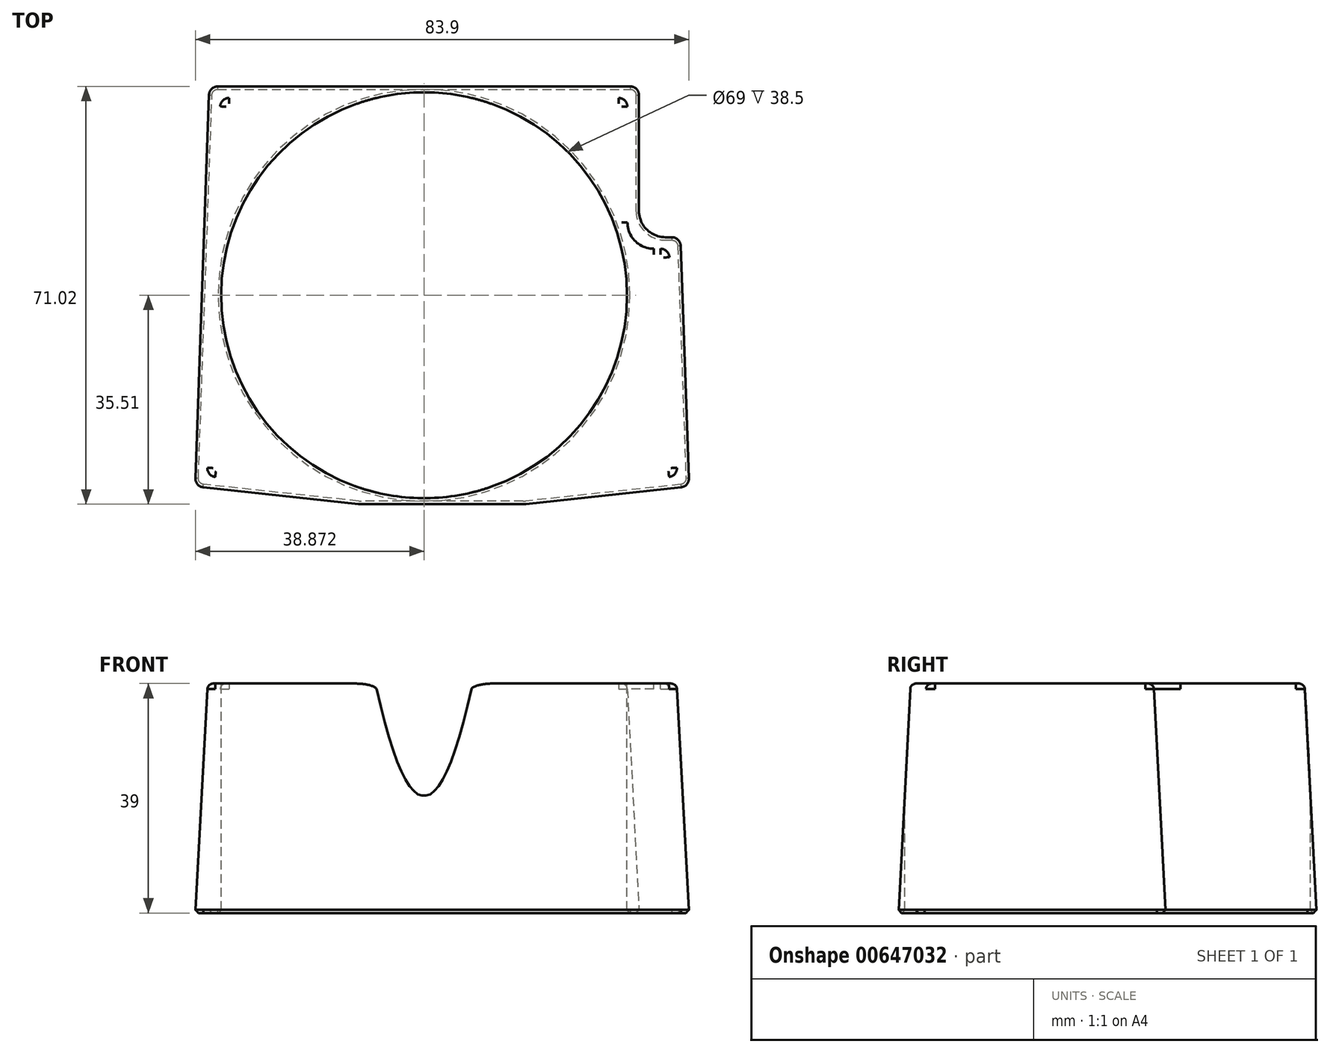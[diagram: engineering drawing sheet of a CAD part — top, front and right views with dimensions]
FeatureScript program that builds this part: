
annotation { "Feature Type Name" : "Feature", "Feature Type Description" : "" }
export const myFeature = defineFeature(function(context is Context, id is Id, definition is map)
    precondition{}
    {
        {
            var Q0;
            Q0=qCreatedBy(makeId("Top.planeOp"),FACE);
            var sketch = newSketch(context, id + "F0", { "sketchPlane" : qUnion([Q0])});
            skCircle(sketch, "E0", {"center": v(14.03, -35.08) * mm, "radius": 9.35 * mm});
            skCircle(sketch, "E1", {"center": v(-27.61, -12.6) * mm, "radius": 3.2 * mm});
            skCircle(sketch, "E2", {"center": v(29.9, -58.2) * mm, "radius": 3.2 * mm});
            skLineSegment(sketch, "E3", {"start": v(-40.06, 0) * mm, "end": v(33.94, 0) * mm});
            skLineSegment(sketch, "E4", {"start": v(42.5, -68.93) * mm, "end": v(14.3, -71.97) * mm});
            skLineSegment(sketch, "E5", {"start": v(13.76, -72) * mm, "end": v(-13.76, -72) * mm});
            skLineSegment(sketch, "E6", {"start": v(-14.3, -71.97) * mm, "end": v(-42.5, -68.93) * mm});
            skLineSegment(sketch, "E7", {"start": v(-42.5, -68.93) * mm, "end": v(-40.06, 0) * mm});
            skCircle(sketch, "E8", {"center": v(-27.61, -12.6) * mm, "radius": 1.2 * mm});
            skCircle(sketch, "E9", {"center": v(29.9, -58.2) * mm, "radius": 1.2 * mm});
            skCircle(sketch, "E10", {"center": v(14.03, -35.08) * mm, "radius": 3.1 * mm});
            skLineSegment(sketch, "E11", {"start": v(0, -72) * mm, "end": v(0, 0) * mm, "construction": true});
            skLineSegment(sketch, "E12.MirrorCS", {"start": v(42.5, -68.93) * mm, "end": v(40.06, 0) * mm});
            skLineSegment(sketch, "E13", {"start": v(40.06, 0) * mm, "end": v(33.94, 0) * mm});
            skPoint(sketch, "E14.visualSharp", {"position": v(14.03, -72) * mm});
            skArc(sketch, "E14.filletArc", {"start": v(13.76, -72) * mm, "mid": v(14.03, -72) * mm, "end": v(14.3, -71.97) * mm});
            skPoint(sketch, "E15.visualSharp", {"position": v(-14.03, -72) * mm});
            skArc(sketch, "E15.filletArc", {"start": v(-14.3, -71.97) * mm, "mid": v(-14.03, -72) * mm, "end": v(-13.76, -72) * mm});
            skLineSegment(sketch, "E16", {"start": v(33.94, 0) * mm, "end": v(33.94, -25.65) * mm});
            skLineSegment(sketch, "E17", {"start": v(33.94, -25.65) * mm, "end": v(40.97, -25.65) * mm});
            skLineSegment(sketch, "E18", {"start": v(0, 0) * mm, "end": v(0, 0.97) * mm});
            skSolve(sketch);
        }
        {
            var Q0;
            Q0=makeQuery(id+"F0.imprint","IMPRINT",FACE,{"disambiguationData":[TD([[makeQuery(id+"F0.imprint","IMPRINT",EDGE,{"derivedFrom":sQuery(id+"F0.wireOp",EDGE,"E0")}),-1.0]])]});
            var Q1;
            Q1=makeQuery(id+"F0.imprint","IMPRINT",FACE,{"disambiguationData":[TD([[makeQuery(id+"F0.imprint","IMPRINT",EDGE,{"derivedFrom":sQuery(id+"F0.wireOp",EDGE,"E0")}),1.0]])]});
            var Q2;
            Q2=makeQuery(id+"F0.imprint","IMPRINT",FACE,{"disambiguationData":[TD([[makeQuery(id+"F0.imprint","IMPRINT",EDGE,{"derivedFrom":sQuery(id+"F0.wireOp",EDGE,"E10")}),1.0]])]});
            var Q3;
            Q3=makeQuery(id+"F0.imprint","IMPRINT",FACE,{"disambiguationData":[TD([[makeQuery(id+"F0.imprint","IMPRINT",EDGE,{"derivedFrom":sQuery(id+"F0.wireOp",EDGE,"E8")}),1.0]])]});
            var Q4;
            Q4=makeQuery(id+"F0.imprint","IMPRINT",FACE,{"disambiguationData":[TD([[makeQuery(id+"F0.imprint","IMPRINT",EDGE,{"derivedFrom":sQuery(id+"F0.wireOp",EDGE,"E1")}),1.0]])]});
            var Q5;
            Q5=makeQuery(id+"F0.imprint","IMPRINT",FACE,{"disambiguationData":[TD([[makeQuery(id+"F0.imprint","IMPRINT",EDGE,{"derivedFrom":sQuery(id+"F0.wireOp",EDGE,"E2")}),1.0]])]});
            var Q6;
            Q6=makeQuery(id+"F0.imprint","IMPRINT",FACE,{"disambiguationData":[TD([[makeQuery(id+"F0.imprint","IMPRINT",EDGE,{"derivedFrom":sQuery(id+"F0.wireOp",EDGE,"E9")}),1.0]])]});
            extrude(context, id + "F1", {"entities" : qUnion([Q0, Q1, Q2, Q3, Q4, Q5, Q6]), "oppositeDirection" : true, "depth" : 39 * mm, "offsetDistance" : 25 * mm, "hasDraft" : true, "draftAngle" : 3 * degree});
        }
        {
            var Q0;
            Q0=makeQuery(id+"F1.opExtrude","SWEPT_EDGE",EDGE,{"disambiguationData":[OSD([sQuery(id+"F0.wireOp",EDGE,"E3"),sQuery(id+"F0.wireOp",EDGE,"E7")])]});
            var Q1;
            Q1=makeQuery(id+"F1.opExtrude","SWEPT_EDGE",EDGE,{"disambiguationData":[OSD([sQuery(id+"F0.wireOp",EDGE,"E3"),sQuery(id+"F0.wireOp",EDGE,"E13"),sQuery(id+"F0.wireOp",EDGE,"E16")])]});
            var Q2;
            Q2=makeQuery(id+"F1.opExtrude","SWEPT_EDGE",EDGE,{"disambiguationData":[OSD([sQuery(id+"F0.wireOp",EDGE,"E6"),sQuery(id+"F0.wireOp",EDGE,"E7")])]});
            var Q3;
            Q3=makeQuery(id+"F1.opExtrude","SWEPT_EDGE",EDGE,{"disambiguationData":[OSD([sQuery(id+"F0.wireOp",EDGE,"E4"),sQuery(id+"F0.wireOp",EDGE,"E12.MirrorCS")])]});
            var Q4;
            Q4=makeQuery(id+"F1.opExtrude","SWEPT_EDGE",EDGE,{"disambiguationData":[OSD([sQuery(id+"F0.wireOp",EDGE,"E12.MirrorCS"),sQuery(id+"F0.wireOp",EDGE,"E17")])]});
            fillet(context, id + "F2", {"entities" : qUnion([Q0, Q1, Q2, Q3, Q4]), "radius" : 4 * mm, "tangentPropagation" : true, "allowEdgeOverflow" : false});
        }
        {
            var Q0;
            Q0=makeQuery(id+"F1.opExtrude","SWEPT_EDGE",EDGE,{"disambiguationData":[OSD([sQuery(id+"F0.wireOp",EDGE,"E16"),sQuery(id+"F0.wireOp",EDGE,"E17")])]});
            fillet(context, id + "F3", {"entities" : qUnion([Q0]), "radius" : 2 * mm, "tangentPropagation" : true, "allowEdgeOverflow" : false});
        }
        {
            var Q0;
            Q0=makeQuery(id+"F1.opExtrude","SWEPT_BODY",BODY,{"disambiguationData":[OSD([sQuery(id+"F0.wireOp",EDGE,"E3"),sQuery(id+"F0.wireOp",EDGE,"E4"),sQuery(id+"F0.wireOp",EDGE,"E5"),sQuery(id+"F0.wireOp",EDGE,"E6"),sQuery(id+"F0.wireOp",EDGE,"E7"),sQuery(id+"F0.wireOp",EDGE,"E12.MirrorCS"),sQuery(id+"F0.wireOp",EDGE,"E14.filletArc"),sQuery(id+"F0.wireOp",EDGE,"E15.filletArc"),sQuery(id+"F0.wireOp",EDGE,"E16"),sQuery(id+"F0.wireOp",EDGE,"E17")])]});
            transform(context, id + "F4", {"entities" : qUnion([Q0]), "transformType" : TransformType.TRANSLATION_3D, "dx" : 0 * mm, "dy" : 0 * mm, "dz" : 0 * mm, "makeCopy" : true});
        }
        {
            var Q0;
            Q0=makeQuery(id+"F1.opExtrude","CAP_FACE",FACE,{"disambiguationData":[OSD([sQuery(id+"F0.wireOp",EDGE,"E3"),sQuery(id+"F0.wireOp",EDGE,"E4"),sQuery(id+"F0.wireOp",EDGE,"E5"),sQuery(id+"F0.wireOp",EDGE,"E6"),sQuery(id+"F0.wireOp",EDGE,"E7"),sQuery(id+"F0.wireOp",EDGE,"E12.MirrorCS"),sQuery(id+"F0.wireOp",EDGE,"E14.filletArc"),sQuery(id+"F0.wireOp",EDGE,"E15.filletArc"),sQuery(id+"F0.wireOp",EDGE,"E16"),sQuery(id+"F0.wireOp",EDGE,"E17")])],"isStart":false});
            var Q1;
            Q1=makeQuery(id+"F1.opExtrude","CAP_FACE",FACE,{"disambiguationData":[OSD([sQuery(id+"F0.wireOp",EDGE,"E3"),sQuery(id+"F0.wireOp",EDGE,"E4"),sQuery(id+"F0.wireOp",EDGE,"E5"),sQuery(id+"F0.wireOp",EDGE,"E6"),sQuery(id+"F0.wireOp",EDGE,"E7"),sQuery(id+"F0.wireOp",EDGE,"E12.MirrorCS"),sQuery(id+"F0.wireOp",EDGE,"E14.filletArc"),sQuery(id+"F0.wireOp",EDGE,"E15.filletArc"),sQuery(id+"F0.wireOp",EDGE,"E16"),sQuery(id+"F0.wireOp",EDGE,"E17")])],"isStart":true});
            shell(context, id + "F5", {"entities" : qUnion([Q0, Q1]), "thickness" : 2.5 * mm});
        }
        {
            var Q0;
            Q0=makeQuery(id+"F1.opExtrude","SWEPT_BODY",BODY,{"disambiguationData":[OSD([sQuery(id+"F0.wireOp",EDGE,"E3"),sQuery(id+"F0.wireOp",EDGE,"E4"),sQuery(id+"F0.wireOp",EDGE,"E5"),sQuery(id+"F0.wireOp",EDGE,"E6"),sQuery(id+"F0.wireOp",EDGE,"E7"),sQuery(id+"F0.wireOp",EDGE,"E12.MirrorCS"),sQuery(id+"F0.wireOp",EDGE,"E14.filletArc"),sQuery(id+"F0.wireOp",EDGE,"E15.filletArc"),sQuery(id+"F0.wireOp",EDGE,"E16"),sQuery(id+"F0.wireOp",EDGE,"E17")])]});
            var Q1;
            Q1=makeQuery(id+"F4.opPattern","COPY",BODY,{"derivedFrom":makeQuery(id+"F1.opExtrude","SWEPT_BODY",BODY,{"disambiguationData":[OSD([sQuery(id+"F0.wireOp",EDGE,"E3"),sQuery(id+"F0.wireOp",EDGE,"E4"),sQuery(id+"F0.wireOp",EDGE,"E5"),sQuery(id+"F0.wireOp",EDGE,"E6"),sQuery(id+"F0.wireOp",EDGE,"E7"),sQuery(id+"F0.wireOp",EDGE,"E12.MirrorCS"),sQuery(id+"F0.wireOp",EDGE,"E14.filletArc"),sQuery(id+"F0.wireOp",EDGE,"E15.filletArc"),sQuery(id+"F0.wireOp",EDGE,"E16"),sQuery(id+"F0.wireOp",EDGE,"E17")])]}),"instanceName":"1"});
            booleanBodies(context, id + "F6", {"operationType" : BooleanOperationType.SUBTRACTION, "tools" : qUnion([Q0]), "targets" : qUnion([Q1])});
        }
        {
            var Q0;
            Q0=makeQuery(id+"F4.opPattern","COPY",FACE,{"derivedFrom":makeQuery(id+"F1.opExtrude","CAP_FACE",FACE,{"disambiguationData":[OSD([sQuery(id+"F0.wireOp",EDGE,"E3"),sQuery(id+"F0.wireOp",EDGE,"E4"),sQuery(id+"F0.wireOp",EDGE,"E5"),sQuery(id+"F0.wireOp",EDGE,"E6"),sQuery(id+"F0.wireOp",EDGE,"E7"),sQuery(id+"F0.wireOp",EDGE,"E12.MirrorCS"),sQuery(id+"F0.wireOp",EDGE,"E14.filletArc"),sQuery(id+"F0.wireOp",EDGE,"E15.filletArc"),sQuery(id+"F0.wireOp",EDGE,"E16"),sQuery(id+"F0.wireOp",EDGE,"E17")])],"isStart":true}),"instanceName":"1"});
            fillet(context, id + "F7", {"entities" : qUnion([Q0]), "radius" : 1 * mm, "tangentPropagation" : true, "allowEdgeOverflow" : false});
        }
        {
            var Q0;
            Q0=makeQuery(id+"F4.opPattern","COPY",FACE,{"derivedFrom":makeQuery(id+"F1.opExtrude","CAP_FACE",FACE,{"disambiguationData":[OSD([sQuery(id+"F0.wireOp",EDGE,"E3"),sQuery(id+"F0.wireOp",EDGE,"E4"),sQuery(id+"F0.wireOp",EDGE,"E5"),sQuery(id+"F0.wireOp",EDGE,"E6"),sQuery(id+"F0.wireOp",EDGE,"E7"),sQuery(id+"F0.wireOp",EDGE,"E12.MirrorCS"),sQuery(id+"F0.wireOp",EDGE,"E14.filletArc"),sQuery(id+"F0.wireOp",EDGE,"E15.filletArc"),sQuery(id+"F0.wireOp",EDGE,"E16"),sQuery(id+"F0.wireOp",EDGE,"E17")])],"isStart":true}),"instanceName":"1"});
            var sketch = newSketch(context, id + "F8", { "sketchPlane" : qUnion([Q0])});
            skLineSegment(sketch, "E19", {"start": v(-25.04, -145.86) * mm, "end": v(-25.04, -78.37) * mm, "construction": true});
            skCircle(sketch, "E20", {"center": v(-25.04, -112.12) * mm, "radius": 34.5 * mm});
            skLineSegment(sketch, "E21.0", {"start": v(11.38, -78.37) * mm, "end": v(-61.45, -78.37) * mm, "construction": true});
            skLineSegment(sketch, "E22.0", {"start": v(-38.8, -145.86) * mm, "end": v(-11.28, -145.86) * mm, "construction": true});
            skLineSegment(sketch, "E23", {"start": v(-3.08, -68.55) * mm, "end": v(-3.08, -3.45) * mm, "construction": true});
            skCircle(sketch, "E24", {"center": v(-3.08, -36) * mm, "radius": 34.5 * mm});
            skSolve(sketch);
        }
        {
            var Q0;
            Q0 = qSketchRegion(id + "F8", true);
            extrude(context, id + "F9", {"entities" : qUnion([Q0]), "operationType" : NewBodyOperationType.REMOVE, "endBound" : BoundingType.THROUGH_ALL, "oppositeDirection" : true, "depth" : 25 * mm, "offsetDistance" : 25 * mm});
        }
        {
            var Q0;
            Q0=makeQuery(id+"F4.opPattern","COPY",FACE,{"derivedFrom":makeQuery(id+"F1.opExtrude","CAP_FACE",FACE,{"disambiguationData":[OSD([sQuery(id+"F0.wireOp",EDGE,"E3"),sQuery(id+"F0.wireOp",EDGE,"E4"),sQuery(id+"F0.wireOp",EDGE,"E5"),sQuery(id+"F0.wireOp",EDGE,"E6"),sQuery(id+"F0.wireOp",EDGE,"E7"),sQuery(id+"F0.wireOp",EDGE,"E12.MirrorCS"),sQuery(id+"F0.wireOp",EDGE,"E14.filletArc"),sQuery(id+"F0.wireOp",EDGE,"E15.filletArc"),sQuery(id+"F0.wireOp",EDGE,"E16"),sQuery(id+"F0.wireOp",EDGE,"E17")])],"isStart":false}),"instanceName":"1"});
            chamfer(context, id + "F10", {"entities" : qUnion([Q0]), "width" : .5 * mm, "tangentPropagation" : true});
        }
    });
